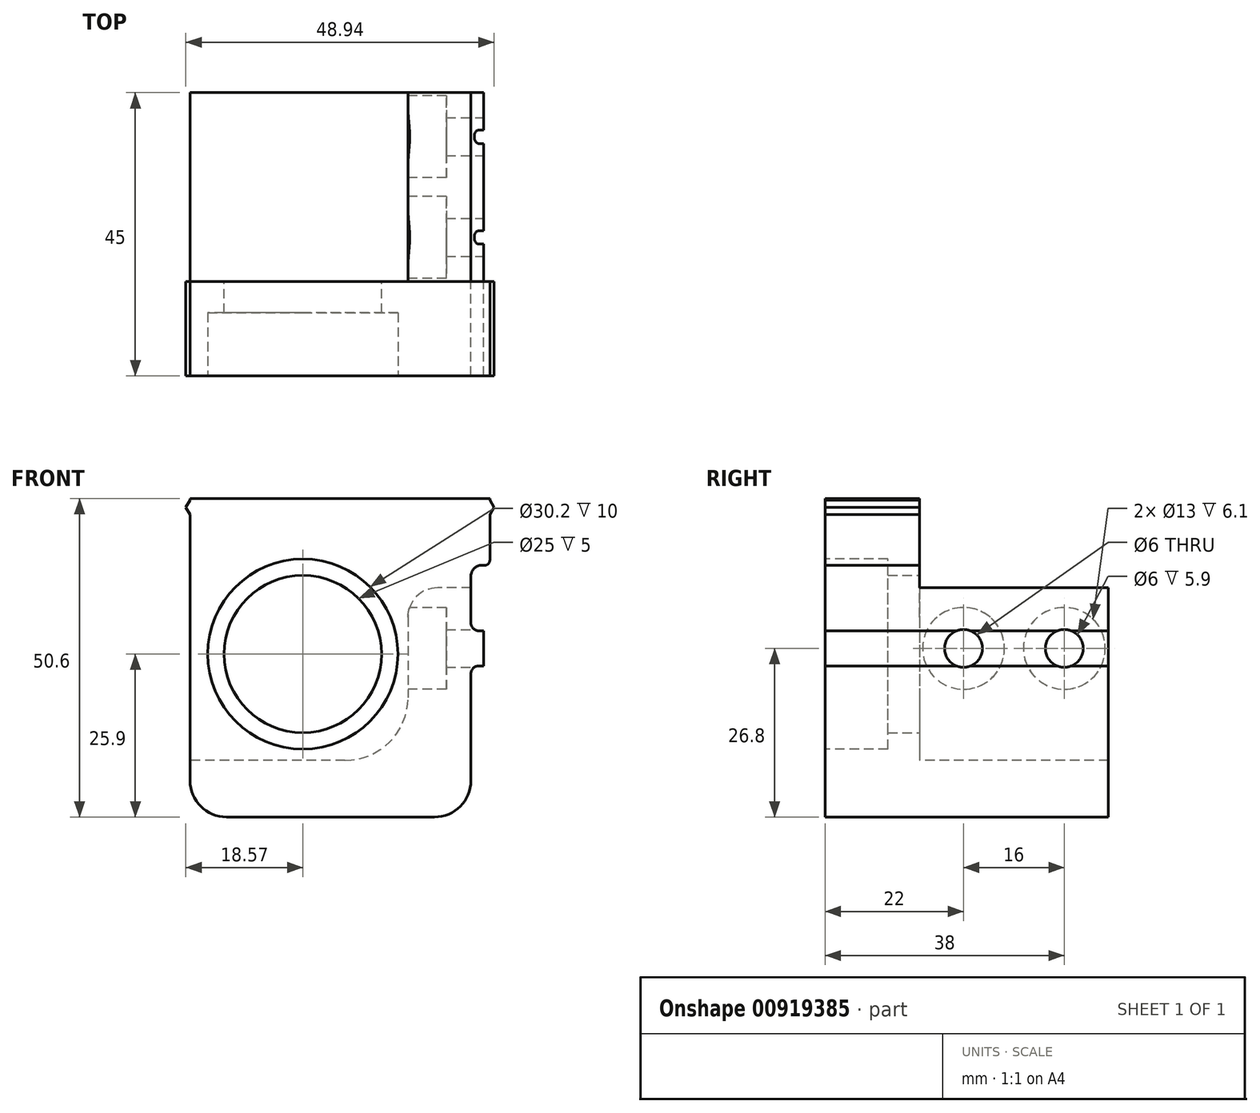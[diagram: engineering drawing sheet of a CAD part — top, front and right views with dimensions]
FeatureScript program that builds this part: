
annotation { "Feature Type Name" : "Feature", "Feature Type Description" : "" }
export const myFeature = defineFeature(function(context is Context, id is Id, definition is map)
    precondition{}
    {
        {
            var Q0;
            Q0=qCreatedBy(makeId("Front.planeOp"),FACE);
            var sketch = newSketch(context, id + "F0", { "sketchPlane" : qUnion([Q0])});
            skLineSegment(sketch, "E0.0", {"start": v(-23.7, 23.56) * mm, "end": v(-23.7, 23.8) * mm});
            skLineSegment(sketch, "E0.1", {"start": v(-24.37, 22.4) * mm, "end": v(-23.7, 23.56) * mm});
            skLineSegment(sketch, "E0.2", {"start": v(-23.7, 21.24) * mm, "end": v(-24.37, 22.4) * mm});
            skLineSegment(sketch, "E0.3", {"start": v(-23.7, -21) * mm, "end": v(-23.7, 21.24) * mm});
            skArc(sketch, "E0.4", {"start": v(-23.7, -21) * mm, "mid": v(-22, -25.1) * mm, "end": v(-17.9, -26.8) * mm});
            skLineSegment(sketch, "E0.5", {"start": v(-23.7, 23.8) * mm, "end": v(23.9, 23.8) * mm});
            skLineSegment(sketch, "E0.6", {"start": v(15.1, -26.8) * mm, "end": v(-17.9, -26.8) * mm});
            skArc(sketch, "E0.7", {"start": v(15.1, -26.8) * mm, "mid": v(19.2, -25.1) * mm, "end": v(20.9, -21) * mm});
            skLineSegment(sketch, "E0.8", {"start": v(20.9, -4) * mm, "end": v(20.9, -21) * mm});
            skArc(sketch, "E0.9", {"start": v(22.1, -2.8) * mm, "mid": v(21.25, -3.15) * mm, "end": v(20.9, -4) * mm});
            skLineSegment(sketch, "E0.10", {"start": v(22.9, -2.8) * mm, "end": v(22.1, -2.8) * mm});
            skLineSegment(sketch, "E0.11", {"start": v(22.9, -2.8) * mm, "end": v(22.9, 2.8) * mm});
            skLineSegment(sketch, "E0.12", {"start": v(23.9, 21.24) * mm, "end": v(23.9, 14) * mm});
            skLineSegment(sketch, "E0.13", {"start": v(24.57, 22.4) * mm, "end": v(23.9, 21.24) * mm});
            skLineSegment(sketch, "E0.14", {"start": v(23.9, 23.56) * mm, "end": v(24.57, 22.4) * mm});
            skLineSegment(sketch, "E0.15", {"start": v(23.9, 23.8) * mm, "end": v(23.9, 23.56) * mm});
            skArc(sketch, "E0.16", {"start": v(23.1, 13.2) * mm, "mid": v(23.67, 13.43) * mm, "end": v(23.9, 14) * mm});
            skLineSegment(sketch, "E0.17", {"start": v(23.1, 13.2) * mm, "end": v(22.6, 13.2) * mm});
            skArc(sketch, "E0.18", {"start": v(22.6, 13.2) * mm, "mid": v(21.4, 12.7) * mm, "end": v(20.9, 11.5) * mm});
            skLineSegment(sketch, "E0.19", {"start": v(20.9, 11.5) * mm, "end": v(20.9, 4) * mm});
            skArc(sketch, "E0.20", {"start": v(20.9, 4) * mm, "mid": v(21.25, 3.15) * mm, "end": v(22.1, 2.8) * mm});
            skLineSegment(sketch, "E0.21", {"start": v(22.1, 2.8) * mm, "end": v(22.9, 2.8) * mm});
            skSolve(sketch);
        }
        {
            var Q0;
            Q0=qSketchRegion(id+"F0",true);
            extrude(context, id + "F1", {"entities" : qUnion([Q0]), "depth" : 55 * mm, "offsetDistance" : 25 * mm});
        }
        {
            var Q0;
            Q0=makeQuery(id+"F1.opExtrude","CAP_FACE",FACE,{"disambiguationData":[OSD([sQuery(id+"F0.wireOp",EDGE,"E0.0"),sQuery(id+"F0.wireOp",EDGE,"E0.1"),sQuery(id+"F0.wireOp",EDGE,"E0.2"),sQuery(id+"F0.wireOp",EDGE,"E0.3"),sQuery(id+"F0.wireOp",EDGE,"E0.4"),sQuery(id+"F0.wireOp",EDGE,"E0.5"),sQuery(id+"F0.wireOp",EDGE,"E0.6"),sQuery(id+"F0.wireOp",EDGE,"E0.7"),sQuery(id+"F0.wireOp",EDGE,"E0.8"),sQuery(id+"F0.wireOp",EDGE,"E0.9"),sQuery(id+"F0.wireOp",EDGE,"E0.10"),sQuery(id+"F0.wireOp",EDGE,"E0.11"),sQuery(id+"F0.wireOp",EDGE,"E0.12"),sQuery(id+"F0.wireOp",EDGE,"E0.13"),sQuery(id+"F0.wireOp",EDGE,"E0.14"),sQuery(id+"F0.wireOp",EDGE,"E0.15"),sQuery(id+"F0.wireOp",EDGE,"E0.16"),sQuery(id+"F0.wireOp",EDGE,"E0.17"),sQuery(id+"F0.wireOp",EDGE,"E0.18"),sQuery(id+"F0.wireOp",EDGE,"E0.19"),sQuery(id+"F0.wireOp",EDGE,"E0.20"),sQuery(id+"F0.wireOp",EDGE,"E0.21")])],"isStart":true});
            var sketch = newSketch(context, id + "F2", { "sketchPlane" : qUnion([Q0])});
            skLineSegment(sketch, "E1", {"start": v(27.02, -17.8) * mm, "end": v(27.02, 29.1) * mm});
            skLineSegment(sketch, "E2.MirrorCS", {"start": v(-9.73, -17.8) * mm, "end": v(-10.9, -17.8) * mm});
            skLineSegment(sketch, "E3.MirrorCS", {"start": v(-10.9, -12.18) * mm, "end": v(-10.9, -17.8) * mm});
            skArc(sketch, "E4.MirrorCS", {"start": v(-15.59, 9.63) * mm, "mid": v(-12.27, 8.26) * mm, "end": v(-10.9, 4.94) * mm});
            skLineSegment(sketch, "E5.MirrorCS", {"start": v(27.02, 29.1) * mm, "end": v(-25.7, 29.1) * mm});
            skLineSegment(sketch, "E6.MirrorCS", {"start": v(-9.73, -17.8) * mm, "end": v(27.02, -17.8) * mm});
            skLineSegment(sketch, "E7.MirrorCS", {"start": v(-10.9, 4.94) * mm, "end": v(-10.9, -12.18) * mm});
            skLineSegment(sketch, "E8.MirrorCS", {"start": v(-25.7, 29.1) * mm, "end": v(-25.7, 9.63) * mm});
            skLineSegment(sketch, "E9.MirrorCS", {"start": v(-25.7, 9.63) * mm, "end": v(-15.59, 9.63) * mm});
            skPoint(sketch, "E10.MirrorP", {"position": v(-14.41, 11.62) * mm});
            skPoint(sketch, "E11.MirrorP", {"position": v(-10.9, -17.8) * mm});
            skSolve(sketch);
        }
        {
            var Q0;
            Q0=qSketchRegion(id+"F2",true);
            extrude(context, id + "F3", {"entities" : qUnion([Q0]), "operationType" : NewBodyOperationType.REMOVE, "oppositeDirection" : true, "depth" : 30 * mm, "offsetDistance" : 25 * mm});
        }
        {
            var Q0;
            Q0=makeQuery(id+"F1.opExtrude","SWEPT_FACE",FACE,{"disambiguationData":[OSD([sQuery(id+"F0.wireOp",EDGE,"E0.11")])]});
            var sketch = newSketch(context, id + "F4", { "sketchPlane" : qUnion([Q0])});
            skCircle(sketch, "E12", {"center": v(-7, 0) * mm, "radius": 3 * mm});
            skCircle(sketch, "E13", {"center": v(-23, 0) * mm, "radius": 3 * mm});
            skSolve(sketch);
        }
        {
            var Q0;
            Q0=qSketchRegion(id+"F4",true);
            extrude(context, id + "F5", {"entities" : qUnion([Q0]), "operationType" : NewBodyOperationType.REMOVE, "oppositeDirection" : true, "depth" : 25 * mm, "offsetDistance" : 25 * mm});
        }
        {
            var Q0;
            Q0=makeQuery(id+"F1.opExtrude","CAP_FACE",FACE,{"disambiguationData":[OSD([sQuery(id+"F0.wireOp",EDGE,"E0.0"),sQuery(id+"F0.wireOp",EDGE,"E0.1"),sQuery(id+"F0.wireOp",EDGE,"E0.2"),sQuery(id+"F0.wireOp",EDGE,"E0.3"),sQuery(id+"F0.wireOp",EDGE,"E0.4"),sQuery(id+"F0.wireOp",EDGE,"E0.5"),sQuery(id+"F0.wireOp",EDGE,"E0.6"),sQuery(id+"F0.wireOp",EDGE,"E0.7"),sQuery(id+"F0.wireOp",EDGE,"E0.8"),sQuery(id+"F0.wireOp",EDGE,"E0.9"),sQuery(id+"F0.wireOp",EDGE,"E0.10"),sQuery(id+"F0.wireOp",EDGE,"E0.11"),sQuery(id+"F0.wireOp",EDGE,"E0.12"),sQuery(id+"F0.wireOp",EDGE,"E0.13"),sQuery(id+"F0.wireOp",EDGE,"E0.14"),sQuery(id+"F0.wireOp",EDGE,"E0.15"),sQuery(id+"F0.wireOp",EDGE,"E0.16"),sQuery(id+"F0.wireOp",EDGE,"E0.17"),sQuery(id+"F0.wireOp",EDGE,"E0.18"),sQuery(id+"F0.wireOp",EDGE,"E0.19"),sQuery(id+"F0.wireOp",EDGE,"E0.20"),sQuery(id+"F0.wireOp",EDGE,"E0.21")])],"isStart":true});
            var sketch = newSketch(context, id + "F6", { "sketchPlane" : qUnion([Q0])});
            skCircle(sketch, "E14", {"center": v(5.8, -0.9) * mm, "radius": 12.5 * mm});
            skLineSegment(sketch, "E15.bottom", {"start": v(-10.7, 22.1) * mm, "end": v(22.3, 22.1) * mm, "construction": true});
            skLineSegment(sketch, "E15.top", {"start": v(-10.7, -23.9) * mm, "end": v(22.3, -23.9) * mm, "construction": true});
            skLineSegment(sketch, "E15.left", {"start": v(-10.7, 22.1) * mm, "end": v(-10.7, -23.9) * mm, "construction": true});
            skLineSegment(sketch, "E15.right", {"start": v(22.3, 22.1) * mm, "end": v(22.3, -23.9) * mm, "construction": true});
            skSolve(sketch);
        }
        {
            var Q0;
            Q0=qSketchRegion(id+"F6",true);
            extrude(context, id + "F7", {"entities" : qUnion([Q0]), "operationType" : NewBodyOperationType.REMOVE, "endBound" : BoundingType.THROUGH_ALL, "oppositeDirection" : true, "depth" : 25 * mm, "offsetDistance" : 25 * mm});
        }
        {
            var Q0;
            Q0=makeQuery(id+"F1.opExtrude","CAP_FACE",FACE,{"disambiguationData":[OSD([sQuery(id+"F0.wireOp",EDGE,"E0.0"),sQuery(id+"F0.wireOp",EDGE,"E0.1"),sQuery(id+"F0.wireOp",EDGE,"E0.2"),sQuery(id+"F0.wireOp",EDGE,"E0.3"),sQuery(id+"F0.wireOp",EDGE,"E0.4"),sQuery(id+"F0.wireOp",EDGE,"E0.5"),sQuery(id+"F0.wireOp",EDGE,"E0.6"),sQuery(id+"F0.wireOp",EDGE,"E0.7"),sQuery(id+"F0.wireOp",EDGE,"E0.8"),sQuery(id+"F0.wireOp",EDGE,"E0.9"),sQuery(id+"F0.wireOp",EDGE,"E0.10"),sQuery(id+"F0.wireOp",EDGE,"E0.11"),sQuery(id+"F0.wireOp",EDGE,"E0.12"),sQuery(id+"F0.wireOp",EDGE,"E0.13"),sQuery(id+"F0.wireOp",EDGE,"E0.14"),sQuery(id+"F0.wireOp",EDGE,"E0.15"),sQuery(id+"F0.wireOp",EDGE,"E0.16"),sQuery(id+"F0.wireOp",EDGE,"E0.17"),sQuery(id+"F0.wireOp",EDGE,"E0.18"),sQuery(id+"F0.wireOp",EDGE,"E0.19"),sQuery(id+"F0.wireOp",EDGE,"E0.20"),sQuery(id+"F0.wireOp",EDGE,"E0.21")])],"isStart":false});
            var sketch = newSketch(context, id + "F8", { "sketchPlane" : qUnion([Q0])});
            skCircle(sketch, "E16", {"center": v(-5.8, -0.9) * mm, "radius": 15.1 * mm});
            skSolve(sketch);
        }
        {
            var Q0;
            Q0=qSketchRegion(id+"F8",true);
            extrude(context, id + "F9", {"entities" : qUnion([Q0]), "operationType" : NewBodyOperationType.REMOVE, "oppositeDirection" : true, "depth" : 20 * mm, "offsetDistance" : 25 * mm});
        }
        {
            var Q0;
            Q0=qCreatedBy(makeId("Right.planeOp"),FACE);
            var sketch = newSketch(context, id + "F10", { "sketchPlane" : qUnion([Q0])});
            skCircle(sketch, "E17", {"center": v(-23, 0) * mm, "radius": 6.5 * mm});
            skCircle(sketch, "E18", {"center": v(-7, 0) * mm, "radius": 6.5 * mm});
            skSolve(sketch);
        }
        {
            var Q0;
            Q0=qSketchRegion(id+"F10",true);
            extrude(context, id + "F11", {"entities" : qUnion([Q0]), "operationType" : NewBodyOperationType.REMOVE, "depth" : 17 * mm, "offsetDistance" : 25 * mm});
        }
        {
            var Q0;
            Q0=makeQuery(id+"F3.boolean.opBoolean","COPY",EDGE,{"derivedFrom":makeQuery(id+"F3.opExtrude","SWEPT_EDGE",EDGE,{"disambiguationData":[OSD([sQuery(id+"F2.wireOp",EDGE,"g0vFc0q4-eDjK-jn1j-iYtA-LaPeeErPCNbr"),sQuery(id+"F2.wireOp",EDGE,"1IZOY0gI-moC3-RnOX-OAqM-tMGjIGVPOsvp")])]})});
            var Q1;
            Q1=makeQuery(id+"F3.boolean.opBoolean","COPY",EDGE,{"derivedFrom":makeQuery(id+"F3.opExtrude","SWEPT_EDGE",EDGE,{"disambiguationData":[OSD([sQuery(id+"F2.wireOp",EDGE,"E2.MirrorCS"),sQuery(id+"F2.wireOp",EDGE,"E3.MirrorCS")])]})});
            fillet(context, id + "F12", {"entities" : qUnion([Q0, Q1]), "radius" : 10 * mm, "tangentPropagation" : true, "allowEdgeOverflow" : false});
        }
        {
            var Q0;
            Q0=makeQuery(id+"F1.opExtrude","CAP_FACE",FACE,{"disambiguationData":[OSD([sQuery(id+"F0.wireOp",EDGE,"E0.0"),sQuery(id+"F0.wireOp",EDGE,"E0.1"),sQuery(id+"F0.wireOp",EDGE,"E0.2"),sQuery(id+"F0.wireOp",EDGE,"E0.3"),sQuery(id+"F0.wireOp",EDGE,"E0.4"),sQuery(id+"F0.wireOp",EDGE,"E0.5"),sQuery(id+"F0.wireOp",EDGE,"E0.6"),sQuery(id+"F0.wireOp",EDGE,"E0.7"),sQuery(id+"F0.wireOp",EDGE,"E0.8"),sQuery(id+"F0.wireOp",EDGE,"E0.9"),sQuery(id+"F0.wireOp",EDGE,"E0.10"),sQuery(id+"F0.wireOp",EDGE,"E0.11"),sQuery(id+"F0.wireOp",EDGE,"E0.12"),sQuery(id+"F0.wireOp",EDGE,"E0.13"),sQuery(id+"F0.wireOp",EDGE,"E0.14"),sQuery(id+"F0.wireOp",EDGE,"E0.15"),sQuery(id+"F0.wireOp",EDGE,"E0.16"),sQuery(id+"F0.wireOp",EDGE,"E0.17"),sQuery(id+"F0.wireOp",EDGE,"E0.18"),sQuery(id+"F0.wireOp",EDGE,"E0.19"),sQuery(id+"F0.wireOp",EDGE,"E0.20"),sQuery(id+"F0.wireOp",EDGE,"E0.21")])],"isStart":false});
            var sketch = newSketch(context, id + "F13", { "sketchPlane" : qUnion([Q0])});
            skLineSegment(sketch, "E19.bottom", {"start": v(-29.3, 28.78) * mm, "end": v(33.28, 28.78) * mm});
            skLineSegment(sketch, "E19.top", {"start": v(-29.3, -28.75) * mm, "end": v(33.28, -28.75) * mm});
            skLineSegment(sketch, "E19.left", {"start": v(-29.3, 28.78) * mm, "end": v(-29.3, -28.75) * mm});
            skLineSegment(sketch, "E19.right", {"start": v(33.28, 28.78) * mm, "end": v(33.28, -28.75) * mm});
            skSolve(sketch);
        }
        {
            var Q0;
            Q0 = qSketchRegion(id + "F13", true);
            extrude(context, id + "F14", {"entities" : qUnion([Q0]), "operationType" : NewBodyOperationType.REMOVE, "oppositeDirection" : true, "depth" : 10 * mm, "offsetDistance" : 25 * mm});
        }
    });
